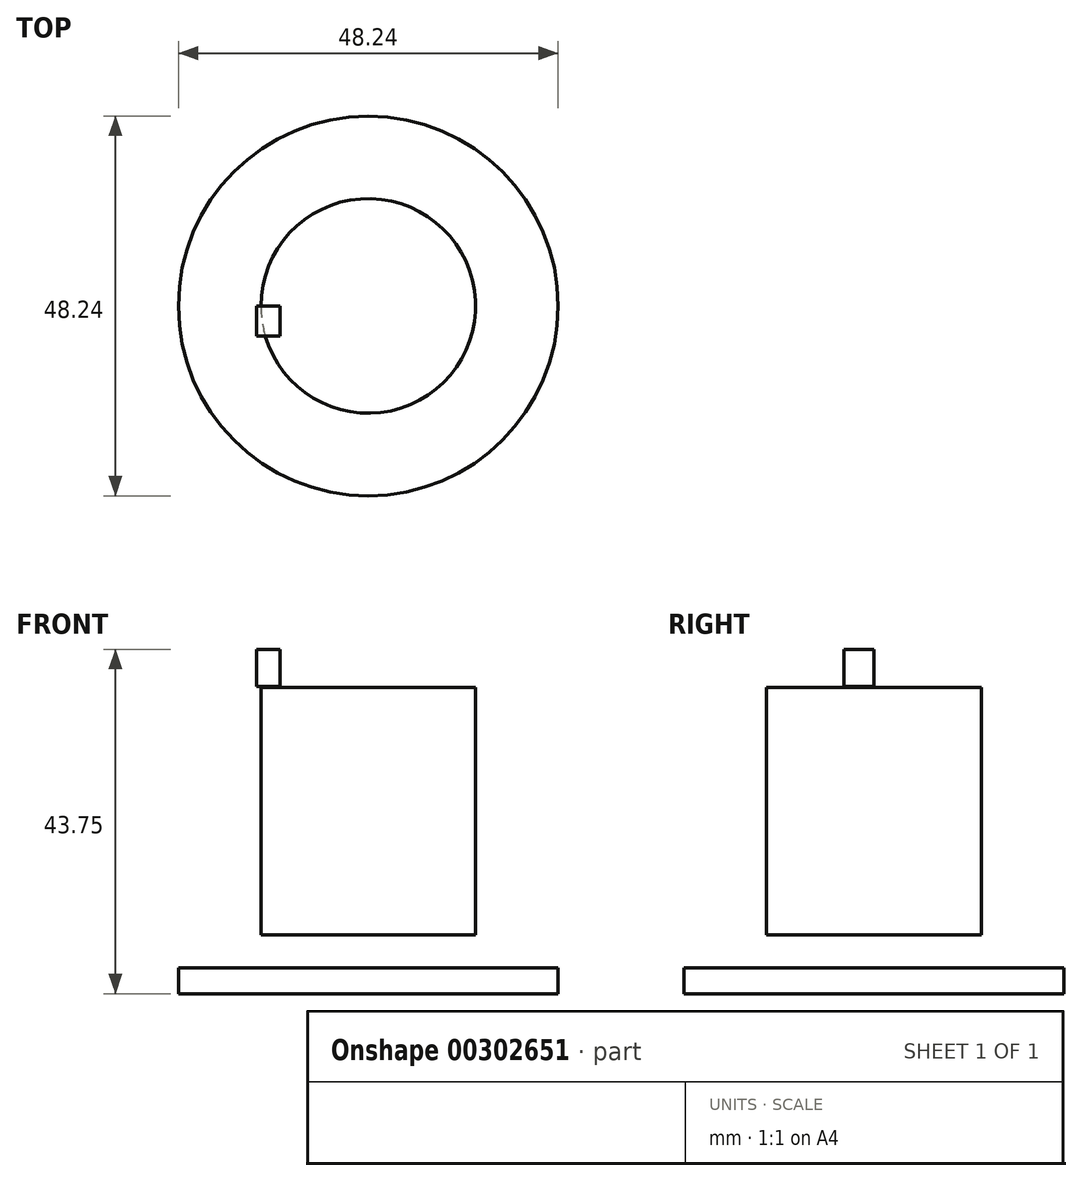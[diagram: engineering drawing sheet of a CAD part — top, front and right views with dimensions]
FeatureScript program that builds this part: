
annotation { "Feature Type Name" : "Feature", "Feature Type Description" : "" }
export const myFeature = defineFeature(function(context is Context, id is Id, definition is map)
    precondition{}
    {
        {
            var Q0;
            Q0=qCreatedBy(makeId("Front.planeOp"),FACE);
            var sketch = newSketch(context, id + "F0", { "sketchPlane" : qUnion([Q0])});
            skLineSegment(sketch, "E0.bottom", {"start": v(0, 0) * mm, "end": v(-24.12, 0) * mm});
            skLineSegment(sketch, "E0.top", {"start": v(0, 3.25) * mm, "end": v(-24.12, 3.25) * mm});
            skLineSegment(sketch, "E0.left", {"start": v(0, 0) * mm, "end": v(0, 3.25) * mm});
            skLineSegment(sketch, "E0.right", {"start": v(-24.12, 0) * mm, "end": v(-24.12, 3.25) * mm});
            skLineSegment(sketch, "E1.bottom", {"start": v(-18.04, 3.25) * mm, "end": v(0, 3.25) * mm});
            skLineSegment(sketch, "E1.top", {"start": v(-18.04, 7.45) * mm, "end": v(0, 7.45) * mm});
            skLineSegment(sketch, "E1.left", {"start": v(-18.04, 3.25) * mm, "end": v(-18.04, 7.45) * mm});
            skLineSegment(sketch, "E1.right", {"start": v(0, 3.25) * mm, "end": v(0, 7.45) * mm});
            skLineSegment(sketch, "E2", {"start": v(0, 7.45) * mm, "end": v(0, 38.9) * mm});
            skLineSegment(sketch, "E3", {"start": v(-13.63, 7.45) * mm, "end": v(-13.63, 38.9) * mm});
            skLineSegment(sketch, "E4", {"start": v(-13.63, 38.9) * mm, "end": v(0, 38.9) * mm});
            skSolve(sketch);
        }
        {
            var Q0;
            {var subQ0=sQuery(id+"F0.wireOp",EDGE,"E2");Q0=makeQuery(id+"F0.imprint","IMPRINT",FACE,{"disambiguationData":[TD([[makeQuery(id+"F0.imprint","IMPRINT",EDGE,{"derivedFrom":subQ0}),1.0]])]});}
            var Q1;
            Q1=makeQuery(id+"F0.imprint","IMPRINT",FACE,{"disambiguationData":[TD([[makeQuery(id+"F0.imprint","IMPRINT",EDGE,{"derivedFrom":sQuery(id+"F0.wireOp",EDGE,"E1.bottom")}),1.0]])]});
            var Q2;
            Q2=makeQuery(id+"F0.imprint","IMPRINT",FACE,{"disambiguationData":[TD([[makeQuery(id+"F0.imprint","IMPRINT",EDGE,{"derivedFrom":sQuery(id+"F0.wireOp",EDGE,"E0.bottom")}),-1.0]])]});
            var Q3;
            Q3=sQuery(id+"F0.wireOp",EDGE,"E2");
            revolve(context, id + "F1", {"entities" : qUnion([Q0, Q1, Q2]), "axis" : qUnion([Q3]), "revolveType" : RevolveType.FULL});
        }
        {
            var Q0;
            Q0=qCreatedBy(makeId("Front.planeOp"),FACE);
            var sketch = newSketch(context, id + "F2", { "sketchPlane" : qUnion([Q0])});
            skLineSegment(sketch, "E5", {"start": v(-14.19, 39.02) * mm, "end": v(-14.19, 43.75) * mm});
            skLineSegment(sketch, "E6", {"start": v(-14.19, 43.75) * mm, "end": v(-11.23, 43.75) * mm});
            skLineSegment(sketch, "E7", {"start": v(-11.23, 39.02) * mm, "end": v(-11.23, 43.75) * mm});
            skLineSegment(sketch, "E8", {"start": v(-11.23, 39.02) * mm, "end": v(-14.19, 39.02) * mm});
            skSolve(sketch);
        }
        {
            var Q0;
            Q0=makeQuery(id+"F2.imprint","IMPRINT",FACE,{"disambiguationData":[TD([[makeQuery(id+"F2.imprint","IMPRINT",EDGE,{"derivedFrom":sQuery(id+"F2.wireOp",EDGE,"E5")}),-1.0]])]});
            extrude(context, id + "F3", {"entities" : qUnion([Q0]), "depth" : 3.8 * mm});
        }
    });
